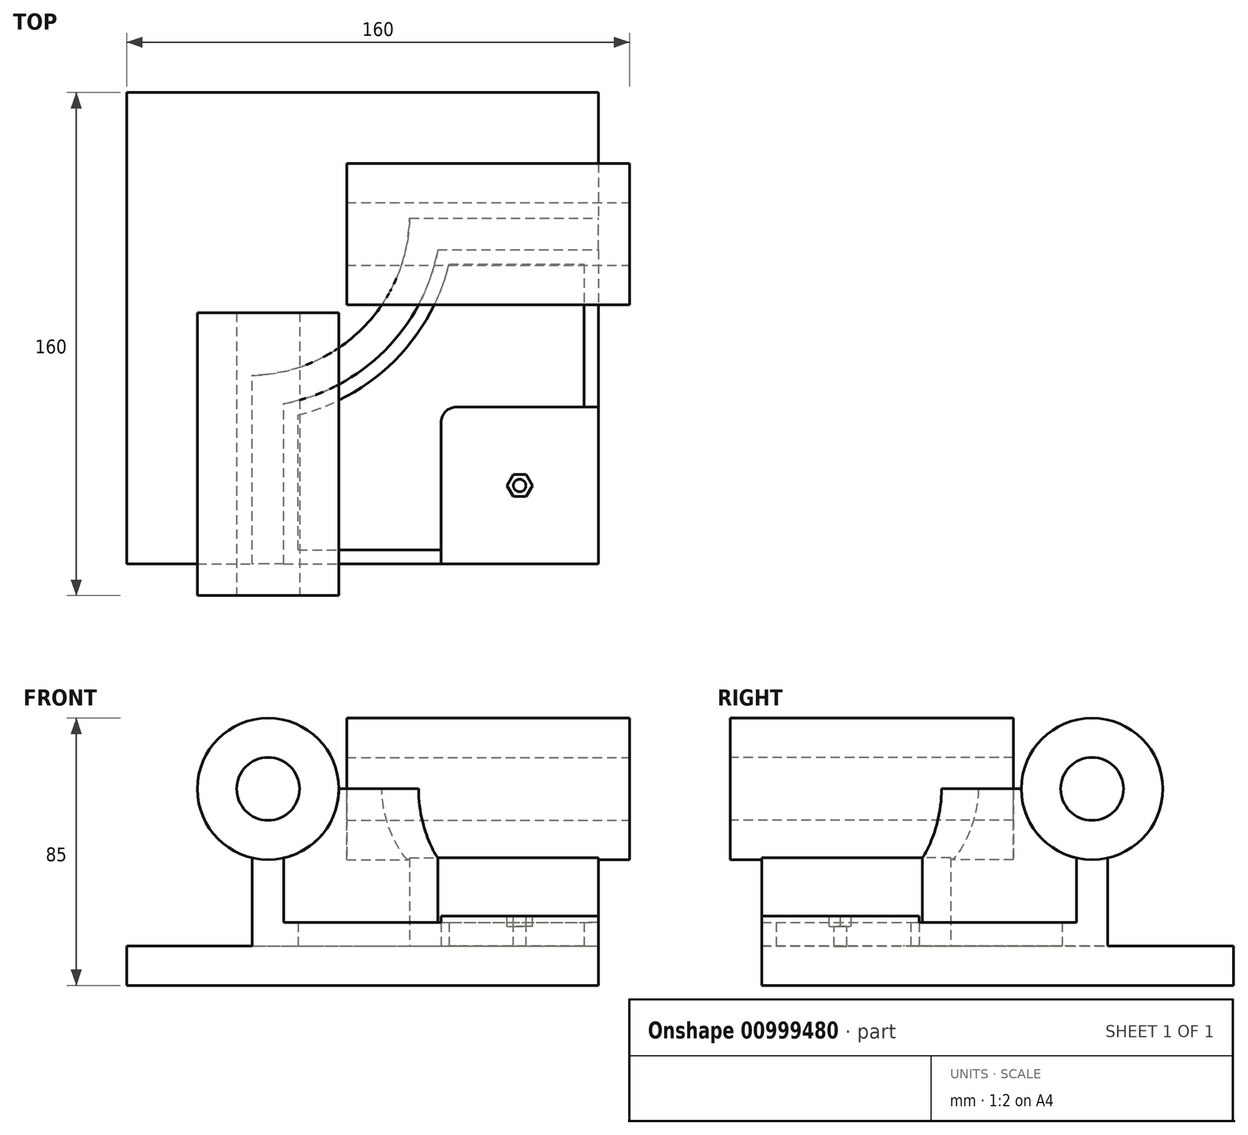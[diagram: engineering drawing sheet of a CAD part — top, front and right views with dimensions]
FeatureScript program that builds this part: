
annotation { "Feature Type Name" : "Feature", "Feature Type Description" : "" }
export const myFeature = defineFeature(function(context is Context, id is Id, definition is map)
    precondition{}
    {
        {
            var Q0;
            Q0=qCreatedBy(makeId("Top.planeOp"),FACE);
            var sketch = newSketch(context, id + "F0", { "sketchPlane" : qUnion([Q0])});
            skLineSegment(sketch, "E0.bottom", {"start": v(-75, 75) * mm, "end": v(75, 75) * mm});
            skLineSegment(sketch, "E0.top", {"start": v(-75, -75) * mm, "end": v(75, -75) * mm});
            skLineSegment(sketch, "E0.left", {"start": v(-75, 75) * mm, "end": v(-75, -75) * mm});
            skLineSegment(sketch, "E0.right", {"start": v(75, 75) * mm, "end": v(75, -75) * mm});
            skPoint(sketch, "E0.middle", {"position": v(0, 0) * mm});
            skSolve(sketch);
        }
        {
            var Q0;
            Q0 = qSketchRegion(id + "F0", true);
            extrude(context, id + "F1", {"entities" : qUnion([Q0]), "depth" : 12.5 * mm, "offsetDistance" : 25 * mm});
        }
        {
            var Q0;
            Q0=makeQuery(id+"F1.opExtrude","CAP_FACE",FACE,{"disambiguationData":[OSD([sQuery(id+"F0.wireOp",EDGE,"E0.bottom"),sQuery(id+"F0.wireOp",EDGE,"E0.top"),sQuery(id+"F0.wireOp",EDGE,"E0.left"),sQuery(id+"F0.wireOp",EDGE,"E0.right")])],"isStart":false});
            var sketch = newSketch(context, id + "F2", { "sketchPlane" : qUnion([Q0])});
            skLineSegment(sketch, "E1", {"start": v(-35, -75) * mm, "end": v(-35, -15) * mm});
            skLineSegment(sketch, "E2", {"start": v(15, 35) * mm, "end": v(75, 35) * mm});
            skArc(sketch, "E3", {"start": v(-35, -15) * mm, "mid": v(0, 0) * mm, "end": v(15, 35) * mm});
            skLineSegment(sketch, "E4.0", {"start": v(23.97, 25) * mm, "end": v(75, 25) * mm});
            skArc(sketch, "E4.1", {"start": v(-25, -23.97) * mm, "mid": v(7.07, -7.07) * mm, "end": v(23.97, 25) * mm});
            skLineSegment(sketch, "E4.2", {"start": v(-25, -75) * mm, "end": v(-25, -23.97) * mm});
            skSolve(sketch);
        }
        {
            var Q0;
            {var subQ3=sQuery(id+"F2.wireOp",EDGE,"E1");Q0=makeQuery(id+"F2.imprint","IMPRINT",FACE,{"disambiguationData":[TD([[makeQuery(id+"F2.imprint","IMPRINT",EDGE,{"derivedFrom":subQ3}),-1.0]])]});}
            extrude(context, id + "F3", {"entities" : qUnion([Q0]), "operationType" : NewBodyOperationType.ADD, "depth" : (12.5 * 4) * mm, "offsetDistance" : 25 * mm});
        }
        {
            var Q0;
            Q0=qCreatedBy(makeId("Front.planeOp"),FACE);
            cPlane(context, id + "F4", {"entities" : qUnion([Q0]), "cplaneType" : CPlaneType.OFFSET, "offset" : 85 * mm, "width" : 150 * mm, "height" : 150 * mm});
        }
        {
            var Q0;
            Q0=qCreatedBy(id+"F4.planeOp",FACE);
            var sketch = newSketch(context, id + "F5", { "sketchPlane" : qUnion([Q0])});
            skCircle(sketch, "E5", {"center": v(-30, 62.5) * mm, "radius": 22.5 * mm});
            skSolve(sketch);
        }
        {
            var Q0;
            Q0 = qSketchRegion(id + "F5", true);
            extrude(context, id + "F6", {"entities" : qUnion([Q0]), "operationType" : NewBodyOperationType.ADD, "oppositeDirection" : true, "depth" : 90 * mm, "offsetDistance" : 25 * mm});
        }
        {
            var Q0;
            Q0=qCreatedBy(makeId("Right.planeOp"),FACE);
            cPlane(context, id + "F7", {"entities" : qUnion([Q0]), "cplaneType" : CPlaneType.OFFSET, "offset" : 85 * mm, "width" : 150 * mm, "height" : 150 * mm});
        }
        {
            var Q0;
            Q0=qCreatedBy(id+"F7.planeOp",FACE);
            var sketch = newSketch(context, id + "F8", { "sketchPlane" : qUnion([Q0])});
            skCircle(sketch, "E6", {"center": v(30, 62.5) * mm, "radius": 22.5 * mm});
            skSolve(sketch);
        }
        {
            var Q0;
            Q0=makeQuery(id+"F8.imprint","IMPRINT",FACE,{"disambiguationData":[TD([[makeQuery(id+"F8.imprint","IMPRINT",EDGE,{"derivedFrom":sQuery(id+"F8.wireOp",EDGE,"E6")}),1.0]])]});
            extrude(context, id + "F9", {"entities" : qUnion([Q0]), "operationType" : NewBodyOperationType.ADD, "oppositeDirection" : true, "depth" : 90 * mm, "offsetDistance" : 25 * mm});
        }
        {
            var Q0;
            {var subQ0=sQuery(id+"F0.wireOp",EDGE,"E0.right");var subQ1=sQuery(id+"F0.wireOp",EDGE,"E0.top");Q0=makeQuery(id+"F3.boolean.opBoolean","SPLIT",FACE,{"disambiguationData":[TD([makeQuery(id+"F3.opExtrude","SWEPT_FACE",FACE,{"disambiguationData":[OSD([sQuery(id+"F2.wireOp",EDGE,"E4.0")])]})])],"derivedFrom":makeQuery(id+"F1.opExtrude","CAP_FACE",FACE,{"disambiguationData":[OSD([sQuery(id+"F0.wireOp",EDGE,"E0.bottom"),subQ1,sQuery(id+"F0.wireOp",EDGE,"E0.left"),subQ0])],"isStart":false})});}
            var sketch = newSketch(context, id + "F10", { "sketchPlane" : qUnion([Q0])});
            skLineSegment(sketch, "E7.bottom", {"start": v(75, -75) * mm, "end": v(25, -75) * mm});
            skLineSegment(sketch, "E7.top", {"start": v(75, -25) * mm, "end": v(30, -25) * mm});
            skLineSegment(sketch, "E7.left", {"start": v(75, -75) * mm, "end": v(75, -25) * mm});
            skLineSegment(sketch, "E7.right", {"start": v(25, -75) * mm, "end": v(25, -30) * mm});
            skPoint(sketch, "E8.visualSharp", {"position": v(25, -25) * mm});
            skArc(sketch, "E8.filletArc", {"start": v(30, -25) * mm, "mid": v(26.46, -26.46) * mm, "end": v(25, -30) * mm});
            skSolve(sketch);
        }
        {
            var Q0;
            Q0 = qSketchRegion(id + "F10", true);
            extrude(context, id + "F11", {"entities" : qUnion([Q0]), "operationType" : NewBodyOperationType.ADD, "depth" : 9.5 * mm, "offsetDistance" : 25 * mm});
        }
        {
            var Q0;
            {var subQ0=sQuery(id+"F0.wireOp",EDGE,"E0.right");var subQ1=sQuery(id+"F0.wireOp",EDGE,"E0.top");Q0=makeQuery(id+"F3.boolean.opBoolean","SPLIT",FACE,{"disambiguationData":[TD([makeQuery(id+"F3.opExtrude","SWEPT_FACE",FACE,{"disambiguationData":[OSD([sQuery(id+"F2.wireOp",EDGE,"E4.0")])]})])],"derivedFrom":makeQuery(id+"F1.opExtrude","CAP_FACE",FACE,{"disambiguationData":[OSD([sQuery(id+"F0.wireOp",EDGE,"E0.bottom"),subQ1,sQuery(id+"F0.wireOp",EDGE,"E0.left"),subQ0])],"isStart":false})});}
            var sketch = newSketch(context, id + "F12", { "sketchPlane" : qUnion([Q0])});
            skLineSegment(sketch, "E9.0", {"start": v(70.5, 20.5) * mm, "end": v(70.5, -25) * mm});
            skLineSegment(sketch, "E9.1", {"start": v(-20.5, -70.5) * mm, "end": v(25, -70.5) * mm});
            skLineSegment(sketch, "E9.2", {"start": v(-20.5, -70.5) * mm, "end": v(-20.5, -27.6) * mm});
            skArc(sketch, "E9.3", {"start": v(-20.5, -27.6) * mm, "mid": v(10.25, -10.25) * mm, "end": v(27.6, 20.5) * mm});
            skLineSegment(sketch, "E9.4", {"start": v(27.6, 20.5) * mm, "end": v(70.5, 20.5) * mm});
            skSolve(sketch);
        }
        {
            var Q0;
            Q0 = qSketchRegion(id + "F12", true);
            var Q1;
            {var subQ11=sQuery(id+"F12.wireOp",EDGE,"E9.0");Q1=makeQuery(id+"F12.imprint","IMPRINT",FACE,{"disambiguationData":[TD([[makeQuery(id+"F12.imprint","IMPRINT",EDGE,{"derivedFrom":subQ11}),1.0]])]});}
            extrude(context, id + "F13", {"entities" : qUnion([Q0, Q1]), "operationType" : NewBodyOperationType.ADD, "depth" : 7.5 * mm, "offsetDistance" : 25 * mm});
        }
        {
            var Q0;
            Q0=makeQuery(id+"F11.opExtrude","CAP_FACE",FACE,{"disambiguationData":[OSD([sQuery(id+"F10.wireOp",EDGE,"E7.bottom"),sQuery(id+"F10.wireOp",EDGE,"E7.top"),sQuery(id+"F10.wireOp",EDGE,"E7.left"),sQuery(id+"F10.wireOp",EDGE,"E7.right"),sQuery(id+"F10.wireOp",EDGE,"E8.filletArc")])],"isStart":false});
            var sketch = newSketch(context, id + "F14", { "sketchPlane" : qUnion([Q0])});
            skCircle(sketch, "E10.cCircle", {"center": v(50, -50) * mm, "radius": 3.5 * mm, "construction": true});
            skPoint(sketch, "E10.cCircle.centerSnap0", {"position": v(50, -75) * mm});
            skPoint(sketch, "E10.cCircle.centerSnap1", {"position": v(75, -50) * mm});
            skLineSegment(sketch, "E10.0", {"start": v(47.98, -46.5) * mm, "end": v(52.02, -46.5) * mm});
            skLineSegment(sketch, "E10.1", {"start": v(52.02, -46.5) * mm, "end": v(54.04, -50) * mm});
            skLineSegment(sketch, "E10.2", {"start": v(54.04, -50) * mm, "end": v(52.02, -53.5) * mm});
            skLineSegment(sketch, "E10.3", {"start": v(52.02, -53.5) * mm, "end": v(47.98, -53.5) * mm});
            skLineSegment(sketch, "E10.4", {"start": v(47.98, -53.5) * mm, "end": v(45.96, -50) * mm});
            skLineSegment(sketch, "E10.5", {"start": v(45.96, -50) * mm, "end": v(47.98, -46.5) * mm});
            skPoint(sketch, "E10.0.midPoint", {"position": v(50, -46.5) * mm});
            skSolve(sketch);
        }
        {
            var Q0;
            Q0 = qSketchRegion(id + "F14", true);
            extrude(context, id + "F15", {"entities" : qUnion([Q0]), "operationType" : NewBodyOperationType.REMOVE, "oppositeDirection" : true, "depth" : 3.2 * mm, "offsetDistance" : 25 * mm});
        }
        {
            var Q0;
            Q0=makeQuery(id+"F15.boolean.opBoolean","COPY",FACE,{"derivedFrom":makeQuery(id+"F15.opExtrude","CAP_FACE",FACE,{"disambiguationData":[OSD([sQuery(id+"F14.wireOp",EDGE,"E10.0"),sQuery(id+"F14.wireOp",EDGE,"E10.1"),sQuery(id+"F14.wireOp",EDGE,"E10.2"),sQuery(id+"F14.wireOp",EDGE,"E10.3"),sQuery(id+"F14.wireOp",EDGE,"E10.4"),sQuery(id+"F14.wireOp",EDGE,"E10.5")])],"isStart":false})});
            var sketch = newSketch(context, id + "F16", { "sketchPlane" : qUnion([Q0])});
            skCircle(sketch, "E11", {"center": v(50, -50) * mm, "radius": 2 * mm});
            skPoint(sketch, "E11.centerSnap0", {"position": v(50, -46.5) * mm});
            skSolve(sketch);
        }
        {
            var Q0;
            Q0 = qSketchRegion(id + "F16", true);
            extrude(context, id + "F17", {"entities" : qUnion([Q0]), "operationType" : NewBodyOperationType.REMOVE, "oppositeDirection" : true, "depth" : 6.4 * mm, "offsetDistance" : 25 * mm});
        }
        {
            var Q0;
            Q0=makeQuery(id+"F6.opExtrude","CAP_FACE",FACE,{"disambiguationData":[OSD([sQuery(id+"F5.wireOp",EDGE,"E5")])],"isStart":true});
            var sketch = newSketch(context, id + "F18", { "sketchPlane" : qUnion([Q0])});
            skCircle(sketch, "E12", {"center": v(-30, 62.5) * mm, "radius": 10 * mm});
            skSolve(sketch);
        }
        {
            var Q0;
            Q0 = qSketchRegion(id + "F18", true);
            extrude(context, id + "F19", {"entities" : qUnion([Q0]), "operationType" : NewBodyOperationType.REMOVE, "endBound" : BoundingType.THROUGH_ALL, "oppositeDirection" : true, "depth" : 25 * mm, "offsetDistance" : 25 * mm});
        }
        {
            var Q0;
            Q0=makeQuery(id+"F9.opExtrude","CAP_FACE",FACE,{"disambiguationData":[OSD([sQuery(id+"F8.wireOp",EDGE,"E6")])],"isStart":true});
            var sketch = newSketch(context, id + "F20", { "sketchPlane" : qUnion([Q0])});
            skCircle(sketch, "E13", {"center": v(30, 62.5) * mm, "radius": 10 * mm});
            skSolve(sketch);
        }
        {
            var Q0;
            Q0 = qSketchRegion(id + "F20", true);
            extrude(context, id + "F21", {"entities" : qUnion([Q0]), "operationType" : NewBodyOperationType.REMOVE, "endBound" : BoundingType.THROUGH_ALL, "oppositeDirection" : true, "depth" : 25 * mm, "offsetDistance" : 25 * mm});
        }
    });
